# Revit family: Luft-Schlammabscheider 1124
name_source: partatom
category: Rohrzubehör
units: mm (PartAtom-declared; Revit-internal decimal feet)

## family parameters
Arbeitsebenenbasiert = Nein
Beim Laden mit Abzugskörper schneiden = Nein
Bemaßung runder Anschluss = Durchmesser verwenden
Gemeinsam genutzt = Nein
Immer vertikal = Ja
OmniClass-Nummer = 23.65.55.14
OmniClass-Titel = Valves for Liquid Services
Teiletyp = Unterbricht

## types (1)
- Luft-Schlammabscheider 1124
    Anwendungsgebiet = Der Luft- und Schlammabscheider wird in der Heizung oder in der Kühlung installiert und dient um Schmutz und Luft aus dem System zu trennen
Einbau in der senkrechten und waagrechte Leitung möglich
    Arbeitsdruck = 600000.0 Pa
    Gehäuse = entzinkungsbeständiges Messing
    H01 = 158.5 mm
    H02 = 92.5 mm
    H03 = 10 mm  [stored 0.0328084 ft]
    H04 = 13.7 mm  [stored 0.0449475 ft]
    H05 = 66 mm  [stored 0.216535 ft]
    H06 = 56 mm  [stored 0.183727 ft]
    H07 = 24 mm  [stored 0.0787402 ft]
    H08 = 17 mm
    H09 = 13.3 mm  [stored 0.0436352 ft]
    H10 = 46 mm  [stored 0.150919 ft]
    H11 = 122 mm
    H12 = 45.2 mm
    H13 = 79.8 mm  [stored 0.261811 ft]
    Hersteller = Herz-Armaturen GmbH
    L01 = 61.9 mm  [stored 0.203084 ft]
    L02 = 70 mm  [stored 0.229659 ft]
    L03 = 102 mm  [stored 0.334646 ft]
    L04 = 49 mm
    R01 = 50.5 mm  [stored 0.165682 ft]
    R02 = 43.5 mm  [stored 0.142717 ft]
    R03 = 14 mm  [stored 0.0459318 ft]
    R04 = 8.3 mm
    R05 = 29 mm  [stored 0.0951444 ft]
    R06 = 21 mm  [stored 0.0688976 ft]
    R07 = 17 mm
    R08 = 34 mm
    R09 = 27.5 mm  [stored 0.0902231 ft]
    R10 = 20 mm  [stored 0.0656168 ft]
    R80 = 20 mm  [stored 0.0656168 ft]
    R90 = 1 mm  [stored 0.00328084 ft]
    R91 = 20.7 mm  [stored 0.0679134 ft]
    R92 = 5 mm  [stored 0.0164042 ft]
    S01 = 33.1 mm
    S02 = 112 mm
    S03 = 86 mm  [stored 0.282152 ft]
    S04 = 112.9 mm
    SCRNCODE = 05;14;02
    SCRNSEQ = AWI;AWI_TYP="1016";2
    T01 = 43 mm  [stored 0.141076 ft]
    URL = www.herz-armaturen.at
    VRL01 = 30 mm  [stored 0.0984252 ft]
    VRL02 = 13 mm
    VRL03 = 18 mm
    VRL04 = 8 mm  [stored 0.0262467 ft]
    VRL05 = 17 mm
    Vorgabe-Ansicht = 0 mm  [stored 0 ft]
    max.Betriebstemperatur (ohne Dampf) = 110 °C
    max.Nenndruck = 1000000.0 Pa

note: [stored X ft] marks values corroborated as IEEE doubles in the binary element streams (Revit-internal decimal feet)
